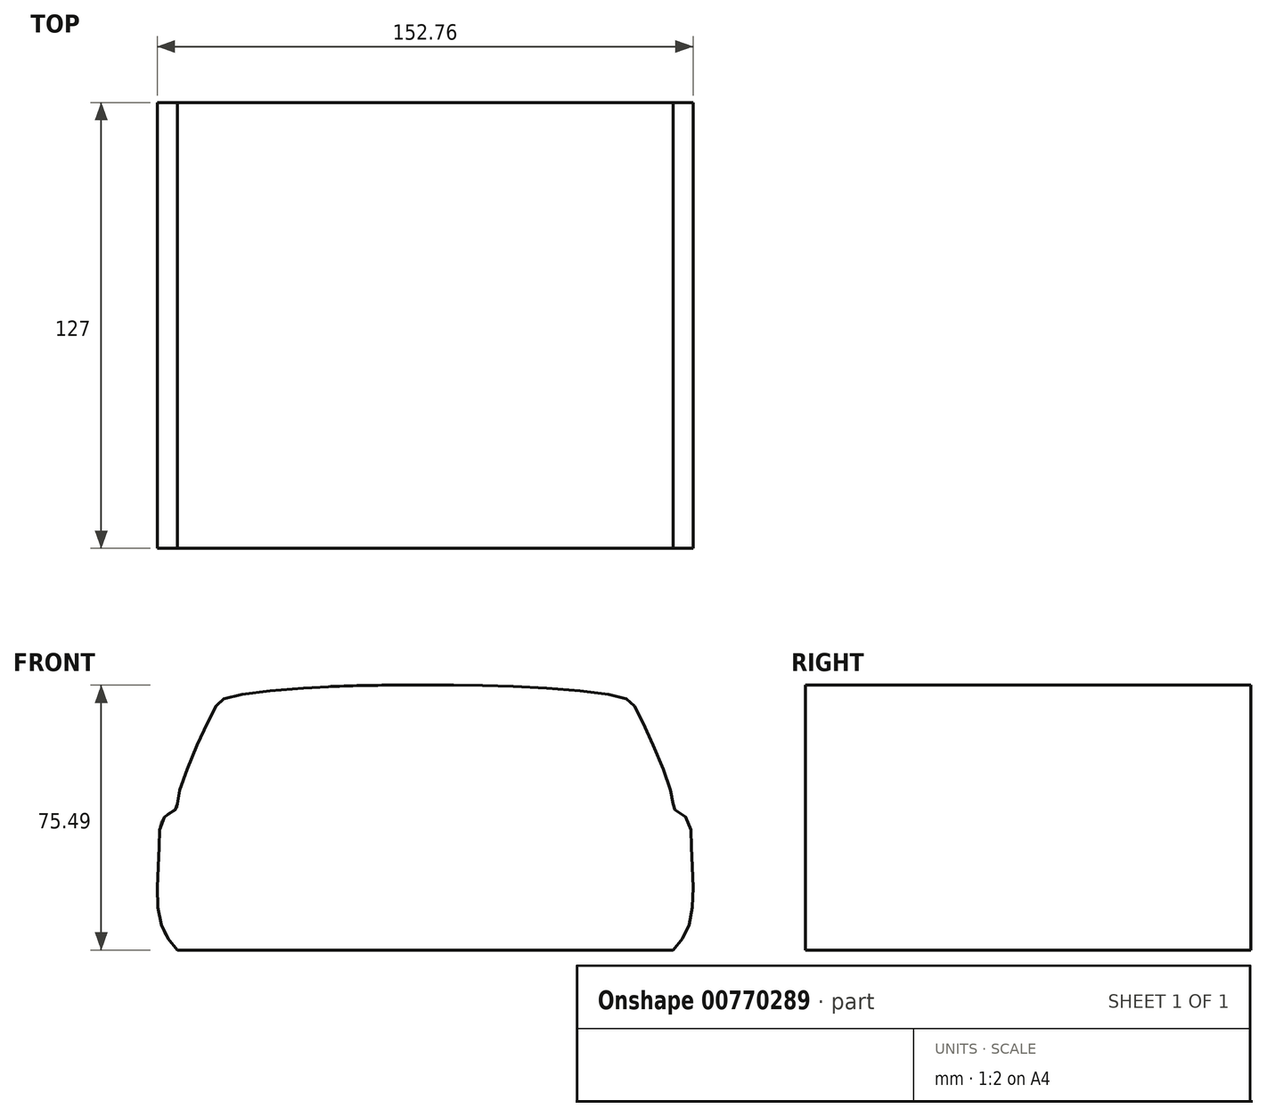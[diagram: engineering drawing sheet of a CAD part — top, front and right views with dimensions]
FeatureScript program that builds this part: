
annotation { "Feature Type Name" : "Feature", "Feature Type Description" : "" }
export const myFeature = defineFeature(function(context is Context, id is Id, definition is map)
    precondition{}
    {
        {
            var Q0;
            Q0=qCreatedBy(makeId("Front.planeOp"),FACE);
            cPlane(context, id + "F0", {"entities" : qUnion([Q0]), "cplaneType" : CPlaneType.OFFSET, "offset" : 25.4 * mm, "width" : 152.4 * mm, "height" : 152.4 * mm});
        }
        {
            var Q0;
            Q0=qCreatedBy(makeId("Front.planeOp"),FACE);
            cPlane(context, id + "F1", {"entities" : qUnion([Q0]), "cplaneType" : CPlaneType.OFFSET, "offset" : 25.4 * mm, "oppositeDirection" : true, "width" : 152.4 * mm, "height" : 152.4 * mm});
        }
        {
            var Q0;
            Q0=qCreatedBy(id+"F0.planeOp",FACE);
            var sketch = newSketch(context, id + "F2", { "sketchPlane" : qUnion([Q0])});
            skLineSegment(sketch, "E0", {"start": v(0, -26.26) * mm, "end": v(70.67, -26.26) * mm});
            skFitSpline(sketch, "E1", {"points": [v(70.67, -26.26) * mm, v(74.82, -20.3) * mm, v(76.38, -9.4) * mm, v(75.86, 4.08) * mm, v(74.56, 11.35) * mm, v(70.67, 14.2) * mm, v(70.67, 15.5) * mm, v(67.3, 26.65) * mm, v(59.78, 42.99) * mm, v(56.67, 45.58) * mm, v(29.44, 48.7) * mm, v(0, 49.21) * mm], "startDerivative": vector(63.3, 71.8) * mm, "endDerivative": vector(-184.05, -0.67) * mm});
            skLineSegment(sketch, "E2.MirrorCS", {"start": v(0, -26.26) * mm, "end": v(-70.67, -26.26) * mm});
            skFitSpline(sketch, "E3.MirrorCS", {"points": [v(-70.67, -26.26) * mm, v(-74.82, -20.3) * mm, v(-76.38, -9.4) * mm, v(-75.86, 4.08) * mm, v(-74.56, 11.35) * mm, v(-70.67, 14.2) * mm, v(-70.67, 15.5) * mm, v(-67.3, 26.65) * mm, v(-59.78, 42.99) * mm, v(-56.67, 45.58) * mm, v(-29.44, 48.7) * mm, v(0, 49.21) * mm], "startDerivative": vector(-63.3, 71.8) * mm, "endDerivative": vector(184.05, -0.67) * mm});
            skSolve(sketch);
        }
        {
            var Q0;
            Q0=qCreatedBy(id+"F1.planeOp",FACE);
            var sketch = newSketch(context, id + "F3", { "sketchPlane" : qUnion([Q0])});
            skLineSegment(sketch, "E4", {"start": v(0, -26.26) * mm, "end": v(70.67, -26.26) * mm});
            skFitSpline(sketch, "E5", {"points": [v(70.67, -26.26) * mm, v(74.82, -20.3) * mm, v(76.38, -9.4) * mm, v(75.86, 4.08) * mm, v(74.56, 11.35) * mm, v(70.67, 14.2) * mm, v(70.67, 15.5) * mm, v(67.3, 26.65) * mm, v(59.78, 42.99) * mm, v(56.67, 45.58) * mm, v(29.44, 48.7) * mm, v(0, 49.21) * mm], "startDerivative": vector(63.3, 71.8) * mm, "endDerivative": vector(-184.05, -0.67) * mm});
            skLineSegment(sketch, "E6.MirrorCS", {"start": v(0, -26.26) * mm, "end": v(-70.67, -26.26) * mm});
            skFitSpline(sketch, "E7.MirrorCS", {"points": [v(-70.67, -26.26) * mm, v(-74.82, -20.3) * mm, v(-76.38, -9.4) * mm, v(-75.86, 4.08) * mm, v(-74.56, 11.35) * mm, v(-70.67, 14.2) * mm, v(-70.67, 15.5) * mm, v(-67.3, 26.65) * mm, v(-59.78, 42.99) * mm, v(-56.67, 45.58) * mm, v(-29.44, 48.7) * mm, v(0, 49.21) * mm], "startDerivative": vector(-63.3, 71.8) * mm, "endDerivative": vector(184.05, -0.67) * mm});
            skSolve(sketch);
        }
        {
            var Q0;
            Q0=qCreatedBy(makeId("Front.planeOp"),FACE);
            var sketch = newSketch(context, id + "F4", { "sketchPlane" : qUnion([Q0])});
            skLineSegment(sketch, "E8", {"start": v(0, -26.26) * mm, "end": v(70.67, -26.26) * mm});
            skFitSpline(sketch, "E9", {"points": [v(70.67, -26.26) * mm, v(74.82, -20.3) * mm, v(76.38, -9.4) * mm, v(75.86, 4.08) * mm, v(74.56, 11.35) * mm, v(70.67, 14.2) * mm, v(70.67, 15.5) * mm, v(67.3, 26.65) * mm, v(59.78, 42.99) * mm, v(56.67, 45.58) * mm, v(29.44, 48.7) * mm, v(0, 49.21) * mm], "startDerivative": vector(63.3, 71.8) * mm, "endDerivative": vector(-184.05, -0.67) * mm});
            skLineSegment(sketch, "E10.MirrorCS", {"start": v(0, -26.26) * mm, "end": v(-70.67, -26.26) * mm});
            skFitSpline(sketch, "E11.MirrorCS", {"points": [v(-70.67, -26.26) * mm, v(-74.82, -20.3) * mm, v(-76.38, -9.4) * mm, v(-75.86, 4.08) * mm, v(-74.56, 11.35) * mm, v(-70.67, 14.2) * mm, v(-70.67, 15.5) * mm, v(-67.3, 26.65) * mm, v(-59.78, 42.99) * mm, v(-56.67, 45.58) * mm, v(-29.44, 48.7) * mm, v(0, 49.21) * mm], "startDerivative": vector(-63.3, 71.8) * mm, "endDerivative": vector(184.05, -0.67) * mm});
            skSolve(sketch);
        }
        {
            var Q0;
            Q0=makeQuery(id+"F2.imprint","IMPRINT",FACE,{"disambiguationData":[TD([[makeQuery(id+"F2.imprint","IMPRINT",EDGE,{"derivedFrom":sQuery(id+"F2.wireOp",EDGE,"E0")}),1.0]])]});
            var Q1;
            Q1=makeQuery(id+"F4.imprint","IMPRINT",FACE,{"disambiguationData":[TD([[makeQuery(id+"F4.imprint","IMPRINT",EDGE,{"derivedFrom":sQuery(id+"F4.wireOp",EDGE,"E8")}),1.0]])]});
            var Q2;
            Q2=makeQuery(id+"F3.imprint","IMPRINT",FACE,{"disambiguationData":[TD([[makeQuery(id+"F3.imprint","IMPRINT",EDGE,{"derivedFrom":sQuery(id+"F3.wireOp",EDGE,"E4")}),1.0]])]});
            loft(context, id + "F5", {"sheetProfilesArray" : [{ "sheetProfileEntities" : qUnion([Q0]) }, { "sheetProfileEntities" : qUnion([Q1]) }, { "sheetProfileEntities" : qUnion([Q2]) }]});
        }
        {
            var Q0;
            Q0=qCreatedBy(makeId("Front.planeOp"),FACE);
            cPlane(context, id + "F6", {"entities" : qUnion([Q0]), "cplaneType" : CPlaneType.OFFSET, "offset" : 50.8 * mm, "oppositeDirection" : true, "width" : 152.4 * mm, "height" : 152.4 * mm});
        }
        {
            var Q0;
            Q0=qCreatedBy(id+"F6.planeOp",FACE);
            var sketch = newSketch(context, id + "F7", { "sketchPlane" : qUnion([Q0])});
            skLineSegment(sketch, "E12", {"start": v(0, -26.26) * mm, "end": v(70.67, -26.26) * mm});
            skFitSpline(sketch, "E13", {"points": [v(70.67, -26.26) * mm, v(74.82, -20.3) * mm, v(76.38, -9.4) * mm, v(75.86, 4.08) * mm, v(74.56, 11.35) * mm, v(70.67, 14.2) * mm, v(70.67, 15.5) * mm, v(67.3, 26.65) * mm, v(59.78, 42.99) * mm, v(56.67, 45.58) * mm, v(29.44, 48.7) * mm, v(0, 49.21) * mm], "startDerivative": vector(63.3, 71.8) * mm, "endDerivative": vector(-184.05, -0.67) * mm});
            skLineSegment(sketch, "E14.MirrorCS", {"start": v(0, -26.26) * mm, "end": v(-70.67, -26.26) * mm});
            skFitSpline(sketch, "E15.MirrorCS", {"points": [v(-70.67, -26.26) * mm, v(-74.82, -20.3) * mm, v(-76.38, -9.4) * mm, v(-75.86, 4.08) * mm, v(-74.56, 11.35) * mm, v(-70.67, 14.2) * mm, v(-70.67, 15.5) * mm, v(-67.3, 26.65) * mm, v(-59.78, 42.99) * mm, v(-56.67, 45.58) * mm, v(-29.44, 48.7) * mm, v(0, 49.21) * mm], "startDerivative": vector(-63.3, 71.8) * mm, "endDerivative": vector(184.05, -0.67) * mm});
            skSolve(sketch);
        }
        {
            var Q0;
            Q0=qCreatedBy(makeId("Front.planeOp"),FACE);
            cPlane(context, id + "F8", {"entities" : qUnion([Q0]), "cplaneType" : CPlaneType.OFFSET, "offset" : 50.8 * mm, "width" : 152.4 * mm, "height" : 152.4 * mm});
        }
        {
            var Q0;
            Q0=qCreatedBy(id+"F8.planeOp",FACE);
            var sketch = newSketch(context, id + "F9", { "sketchPlane" : qUnion([Q0])});
            skLineSegment(sketch, "E16", {"start": v(0, -26.26) * mm, "end": v(70.67, -26.26) * mm});
            skFitSpline(sketch, "E17", {"points": [v(70.67, -26.26) * mm, v(74.82, -20.3) * mm, v(76.38, -9.4) * mm, v(75.86, 4.08) * mm, v(74.56, 11.35) * mm, v(70.67, 14.2) * mm, v(70.67, 15.5) * mm, v(67.3, 26.65) * mm, v(59.78, 42.99) * mm, v(56.67, 45.58) * mm, v(29.44, 48.7) * mm, v(0, 49.21) * mm], "startDerivative": vector(63.3, 71.8) * mm, "endDerivative": vector(-184.05, -0.67) * mm});
            skLineSegment(sketch, "E18.MirrorCS", {"start": v(0, -26.26) * mm, "end": v(-70.67, -26.26) * mm});
            skFitSpline(sketch, "E19.MirrorCS", {"points": [v(-70.67, -26.26) * mm, v(-74.82, -20.3) * mm, v(-76.38, -9.4) * mm, v(-75.86, 4.08) * mm, v(-74.56, 11.35) * mm, v(-70.67, 14.2) * mm, v(-70.67, 15.5) * mm, v(-67.3, 26.65) * mm, v(-59.78, 42.99) * mm, v(-56.67, 45.58) * mm, v(-29.44, 48.7) * mm, v(0, 49.21) * mm], "startDerivative": vector(-63.3, 71.8) * mm, "endDerivative": vector(184.05, -0.67) * mm});
            skSolve(sketch);
        }
        {
            var Q0;
            Q0=qCreatedBy(id+"F8.planeOp",FACE);
            cPlane(context, id + "F10", {"entities" : qUnion([Q0]), "cplaneType" : CPlaneType.OFFSET, "offset" : 25.4 * mm, "width" : 152.4 * mm, "height" : 152.4 * mm});
        }
        {
            var Q0;
            Q0=qCreatedBy(id+"F6.planeOp",FACE);
            cPlane(context, id + "F11", {"entities" : qUnion([Q0]), "cplaneType" : CPlaneType.OFFSET, "offset" : 25.4 * mm, "width" : 152.4 * mm, "height" : 152.4 * mm});
        }
        {
            var Q0;
            Q0=qCreatedBy(id+"F10.planeOp",FACE);
            var sketch = newSketch(context, id + "F12", { "sketchPlane" : qUnion([Q0])});
            skLineSegment(sketch, "E20", {"start": v(0, -26.26) * mm, "end": v(70.67, -26.26) * mm});
            skFitSpline(sketch, "E21", {"points": [v(70.67, -26.26) * mm, v(74.82, -20.3) * mm, v(76.38, -9.4) * mm, v(75.86, 4.08) * mm, v(74.56, 11.35) * mm, v(70.67, 14.2) * mm, v(70.67, 15.5) * mm, v(67.3, 26.65) * mm, v(59.78, 42.99) * mm, v(56.67, 45.58) * mm, v(29.44, 48.7) * mm, v(0, 49.21) * mm], "startDerivative": vector(63.3, 71.8) * mm, "endDerivative": vector(-184.05, -0.67) * mm});
            skLineSegment(sketch, "E22.MirrorCS", {"start": v(0, -26.26) * mm, "end": v(-70.67, -26.26) * mm});
            skFitSpline(sketch, "E23.MirrorCS", {"points": [v(-70.67, -26.26) * mm, v(-74.82, -20.3) * mm, v(-76.38, -9.4) * mm, v(-75.86, 4.08) * mm, v(-74.56, 11.35) * mm, v(-70.67, 14.2) * mm, v(-70.67, 15.5) * mm, v(-67.3, 26.65) * mm, v(-59.78, 42.99) * mm, v(-56.67, 45.58) * mm, v(-29.44, 48.7) * mm, v(0, 49.21) * mm], "startDerivative": vector(-63.3, 71.8) * mm, "endDerivative": vector(184.05, -0.67) * mm});
            skSolve(sketch);
        }
        {
            var Q1;
            Q1=makeQuery(id+"F12.imprint","IMPRINT",FACE,{"disambiguationData":[TD([[makeQuery(id+"F12.imprint","IMPRINT",EDGE,{"derivedFrom":sQuery(id+"F12.wireOp",EDGE,"E20")}),1.0]])]});
            var Q2;
            Q2=makeQuery(id+"F9.imprint","IMPRINT",FACE,{"disambiguationData":[TD([[makeQuery(id+"F9.imprint","IMPRINT",EDGE,{"derivedFrom":sQuery(id+"F9.wireOp",EDGE,"E16")}),1.0]])]});
            var Q3;
            Q3=makeQuery(id+"F7.imprint","IMPRINT",FACE,{"disambiguationData":[TD([[makeQuery(id+"F7.imprint","IMPRINT",EDGE,{"derivedFrom":sQuery(id+"F7.wireOp",EDGE,"E12")}),1.0]])]});
            loft(context, id + "F13", {"operationType" : NewBodyOperationType.ADD, "sheetProfilesArray" : [{ "sheetProfileEntities" : qUnion([Q1]) }, { "sheetProfileEntities" : qUnion([Q2]) }, { "sheetProfileEntities" : qUnion([Q3]) }]});
        }
    });
